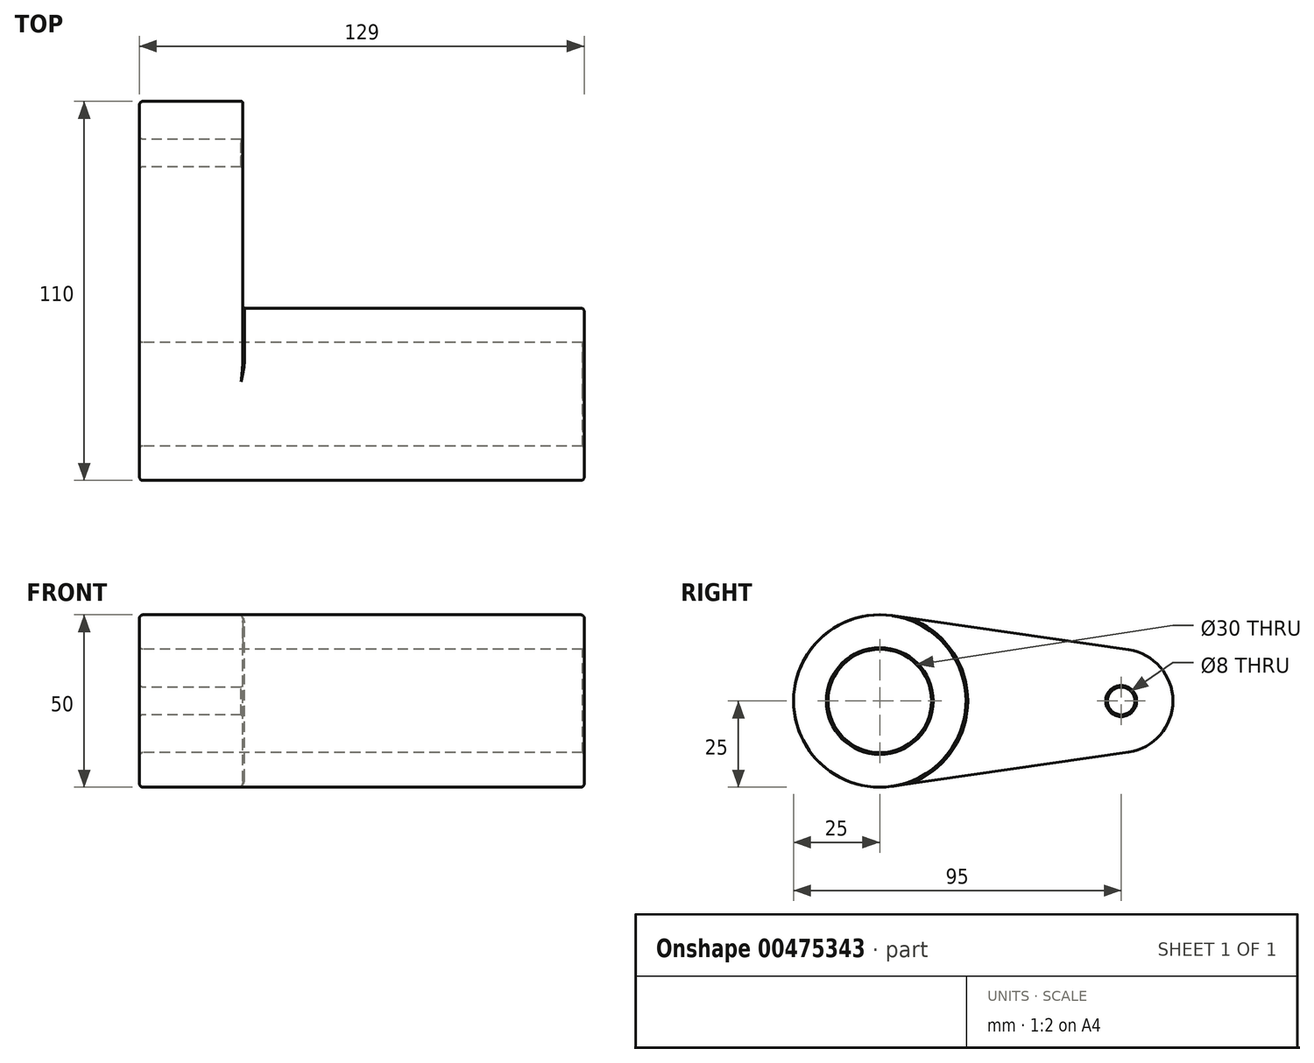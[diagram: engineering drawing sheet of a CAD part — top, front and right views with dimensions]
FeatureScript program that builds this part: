
annotation { "Feature Type Name" : "Feature", "Feature Type Description" : "" }
export const myFeature = defineFeature(function(context is Context, id is Id, definition is map)
    precondition{}
    {
        {
            var Q0;
            Q0=qCreatedBy(makeId("Right.planeOp"),FACE);
            var sketch = newSketch(context, id + "F0", { "sketchPlane" : qUnion([Q0])});
            skCircle(sketch, "E0", {"center": v(0, 0) * mm, "radius": 25 * mm});
            skCircle(sketch, "E1", {"center": v(70, 0) * mm, "radius": 15 * mm});
            skLineSegment(sketch, "E2", {"start": v(3.57, 24.74) * mm, "end": v(72.14, 14.85) * mm});
            skLineSegment(sketch, "E3", {"start": v(3.57, -24.74) * mm, "end": v(72.14, -14.85) * mm});
            skCircle(sketch, "E4", {"center": v(0, 0) * mm, "radius": 15 * mm});
            skCircle(sketch, "E5", {"center": v(70, 0) * mm, "radius": 4 * mm});
            skSolve(sketch);
        }
        {
            var Q0;
            Q0 = qSketchRegion(id + "F0", true);
            extrude(context, id + "F1", {"entities" : qUnion([Q0]), "depth" : 30 * mm, "offsetDistance" : 25 * mm});
        }
        {
            var Q0;
            Q0=makeQuery(id+"F0.imprint","IMPRINT",FACE,{"disambiguationData":[TD([[makeQuery(id+"F0.imprint","IMPRINT",EDGE,{"derivedFrom":sQuery(id+"F0.wireOp",EDGE,"E4")}),-1.0]])]});
            extrude(context, id + "F2", {"entities" : qUnion([Q0]), "operationType" : NewBodyOperationType.ADD, "depth" : 129 * mm, "offsetDistance" : 25 * mm});
        }
        {
            var Q0;
            Q0=makeQuery(id+"F2.opExtrude","CAP_EDGE",EDGE,{"disambiguationData":[OSD([sQuery(id+"F0.wireOp",EDGE,"E0")])],"isStart":false});
            var Q1;
            Q1=makeQuery(id+"F1.opExtrude","CAP_EDGE",EDGE,{"disambiguationData":[OSD([sQuery(id+"F0.wireOp",EDGE,"E3")])],"isStart":true});
            var Q2;
            Q2=makeQuery(id+"F1.opExtrude","CAP_EDGE",EDGE,{"disambiguationData":[OSD([sQuery(id+"F0.wireOp",EDGE,"E1")])],"isStart":true});
            var Q3;
            Q3=makeQuery(id+"F1.opExtrude","CAP_EDGE",EDGE,{"disambiguationData":[OSD([sQuery(id+"F0.wireOp",EDGE,"E0")])],"isStart":true});
            var Q4;
            Q4=makeQuery(id+"F1.opExtrude","CAP_EDGE",EDGE,{"disambiguationData":[OSD([sQuery(id+"F0.wireOp",EDGE,"E2")])],"isStart":true});
            var Q5;
            Q5=makeQuery(id+"F1.opExtrude","CAP_EDGE",EDGE,{"disambiguationData":[OSD([sQuery(id+"F0.wireOp",EDGE,"E4")])],"isStart":true});
            var Q6;
            Q6=makeQuery(id+"F1.opExtrude","CAP_EDGE",EDGE,{"disambiguationData":[OSD([sQuery(id+"F0.wireOp",EDGE,"E5")])],"isStart":true});
            fillet(context, id + "F3", {"entities" : qUnion([Q0, Q1, Q2, Q3, Q4, Q5, Q6]), "radius" : 1 * mm, "tangentPropagation" : true, "allowEdgeOverflow" : false});
        }
        {
            var Q0;
            Q0=makeQuery(id+"F1.opExtrude","CAP_EDGE",EDGE,{"disambiguationData":[OSD([sQuery(id+"F0.wireOp",EDGE,"E2")])],"isStart":false});
            var Q1;
            Q1=makeQuery(id+"F1.opExtrude","CAP_EDGE",EDGE,{"disambiguationData":[OSD([sQuery(id+"F0.wireOp",EDGE,"E1")])],"isStart":false});
            var Q2;
            Q2=makeQuery(id+"F1.opExtrude","CAP_EDGE",EDGE,{"disambiguationData":[OSD([sQuery(id+"F0.wireOp",EDGE,"E3")])],"isStart":false});
            fillet(context, id + "F4", {"entities" : qUnion([Q0, Q1, Q2]), "radius" : 0.5 * mm, "tangentPropagation" : true, "allowEdgeOverflow" : false});
        }
        {
            var Q0;
            {var subQ0=sQuery(id+"F0.wireOp",EDGE,"E0");Q0=makeQuery(id+"F2.boolean.opBoolean","INTERSECT",EDGE,{"derivedFrom":[makeQuery(id+"F1.opExtrude","CAP_FACE",FACE,{"disambiguationData":[OSD([subQ0,sQuery(id+"F0.wireOp",EDGE,"E1"),sQuery(id+"F0.wireOp",EDGE,"E2"),sQuery(id+"F0.wireOp",EDGE,"E3"),sQuery(id+"F0.wireOp",EDGE,"E4"),sQuery(id+"F0.wireOp",EDGE,"E5")])],"isStart":false}),makeQuery(id+"F2.opExtrude","SWEPT_FACE",FACE,{"disambiguationData":[OSD([subQ0])]})]});}
            var Q1;
            Q1=makeQuery(id+"F2.opExtrude","CAP_EDGE",EDGE,{"disambiguationData":[OSD([sQuery(id+"F0.wireOp",EDGE,"E4")])],"isStart":false});
            var Q2;
            Q2=makeQuery(id+"F1.opExtrude","CAP_EDGE",EDGE,{"disambiguationData":[OSD([sQuery(id+"F0.wireOp",EDGE,"E5")])],"isStart":false});
            chamfer(context, id + "F5", {"entities" : qUnion([Q0, Q1, Q2]), "width" : 0.5 * mm, "tangentPropagation" : true});
        }
    });
